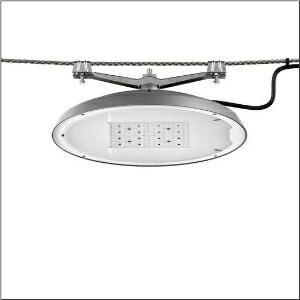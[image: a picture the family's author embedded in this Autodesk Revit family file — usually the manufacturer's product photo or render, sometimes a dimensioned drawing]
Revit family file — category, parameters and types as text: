
# Revit family: dl_50_iq_mini___st0_8s_5xa248v31f08le_de0f
name_source: partatom
category: Lighting Fixtures
units: mm (PartAtom-declared; Revit-internal decimal feet)

## family parameters
Cut with Voids When Loaded = No
Host = Face
Light Source = No
Part Type = Normal
Room Calculation Point = No
Round Connector Dimension = Use Diameter
Shared = No

## types (1)
- --- (1 x LED, 10390 lm, 67.4 W, 3000K)
    Apparent Load = 67 VA
    CIE Flux Codes = 38 75 97 100 100
    Color Rendering = 70
    Color Temperature = 3000K
    Default Elevation = 1800 mm
    Description = DL 50 iQ mini, catenary luminaire, primary light control with lens, of PMMA, primary optical cover: cover, of toughened safety glass, transparent, light distribution: ST0.8s, light emission: direct distribution, primary light characteristic: symmetric, installation type: suspended mounting, LED, High Power LED, rated luminous flux: 10.390lm, luminous efficacy: 154lm/W, light colour: 730, colour temperature: 3000K, control gear: iQ Street-Remote, control: optimised constant luminous flux control (CLO 2.0), Desk-Remote (wireless, voltage-free reading and setting of iQ features in the workshop via application-optimized NFC function/RFID function), Light-Fading, Smart-Wire, Night-Set, Lumen-Switch, Temp-Guard, Auto-Match, Street-Remote, mains connection: 230..240V, AC, 50/60Hz, start of lifetime: 67W, end of service life: 70W, reduction: 31W, luminaire housing, of diecast aluminium, powder-coated, SITECO metallic grey (DB 702S), diameter: 500mm, height: 115mm, mounting height: 4..12m, protection rating (complete): IP66, insulation class (complete): insulation class II (safety insulation), certification: CE, ENEC, ENEC+, VDE, impact resistance: IK08, permissible operating ambient temperature for outdoor applications: -25..+40°C, standard-compliant lighting for roads and squares, packaging unit: 1 piece

Light Distribution: ST0.8s
    Height = 124 mm  [stored 0.406824 ft]
    Lamp = 1 x LED
    Lamp Light Flux = 10390 lm
    Lamp Power = 67.4 W
    Lamp count = 1
    Length = 500 mm
    Luminous efficacy = 154 lm/W
    Manufacturer = Siteco
    ModVariant = No
    Model = 5XA248V31F08LE
    Number of Poles = 1
    OnlyDefault = Yes
    Power Factor = 1
    Product Name = DL 50 iQ mini | ST0.8s
    Product group = catenary luminaire
    ProductGroupID = 6300
    Protection Class = Protection class II
    Protection Degree = IP 66
    RLX_Detail_Level = 1
    RLX_Emergency_Light_Flux = 0 lm
    RLX_Emergency_Type = 0
    RLX_Emergency_Type_DB = No
    RlxData = <blob elided: 127025 chars, md5=472b21f3>
    Socket = socket
    Standby Power = 0 W
    System Light Flux = 10390 lm
    System Power = 67 W
    Type Comments = factory setting: luminous flux: 100 % | dim-lin: 254 | 705 mA
    Type Image = l_1251783.jpg
    URL = http://relux.com
    VarID = @adj_140553
    Voltage = 0 V
    Weight = 0.00 kg
    Width = 0 mm  [stored 0 ft]

note: [stored X ft] marks values corroborated as IEEE doubles in the binary element streams (Revit-internal decimal feet)

## geometry (parser evidence)
native form markers: Blend x4, Sweep x15
no freeform markers — native parametric forms only
